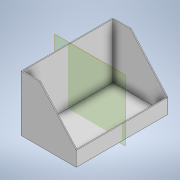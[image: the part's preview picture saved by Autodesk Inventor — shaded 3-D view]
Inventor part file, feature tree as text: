
AUTODESK INVENTOR PART (.ipt)
format: ipt  version: 2022 (Build 260153000, 153)  size: 135,680 bytes
history: native  units: in
note: dims shown in document units (in); Inventor stores cm internally (conversion verified against a paired STEP export)
features: extrude x4, sketch x4, plane x1, mirror x1
ambient origin geometry x8: Origin, YZ Plane, XZ Plane, XY Plane, X Axis, Y Axis, Z Axis, Center Point
bodies: Solid1 (feature_tree)
feature tree (10):
  extrude  "Extrusion1"  Depth=39.3701in
  extrude  "Extrusion2"  Depth=23.622in
  plane  "Work Plane1"
  mirror  "Mirror1"
  extrude  "Extrusion3"  Depth=5.9055in
  extrude  "Extrusion4"  Depth=0.3937in TaperAngle=0.0deg
  sketch  "Sketch2"  dims[d0=23.622in d1=39.3701in]
  sketch  "Sketch3"  dims[d2=0.3937in d3=0.0in d4=23.622in]
  sketch  "Sketch4"  dims[d5=7.874in d6=5.9055in]
  sketch  "Sketch5"  dims[d7=0.3937in d8=0.0in d9=0.3937in d10=0.0in d11=0.3937in d12=0.0in d13=23.622in d14=0.3323in]
